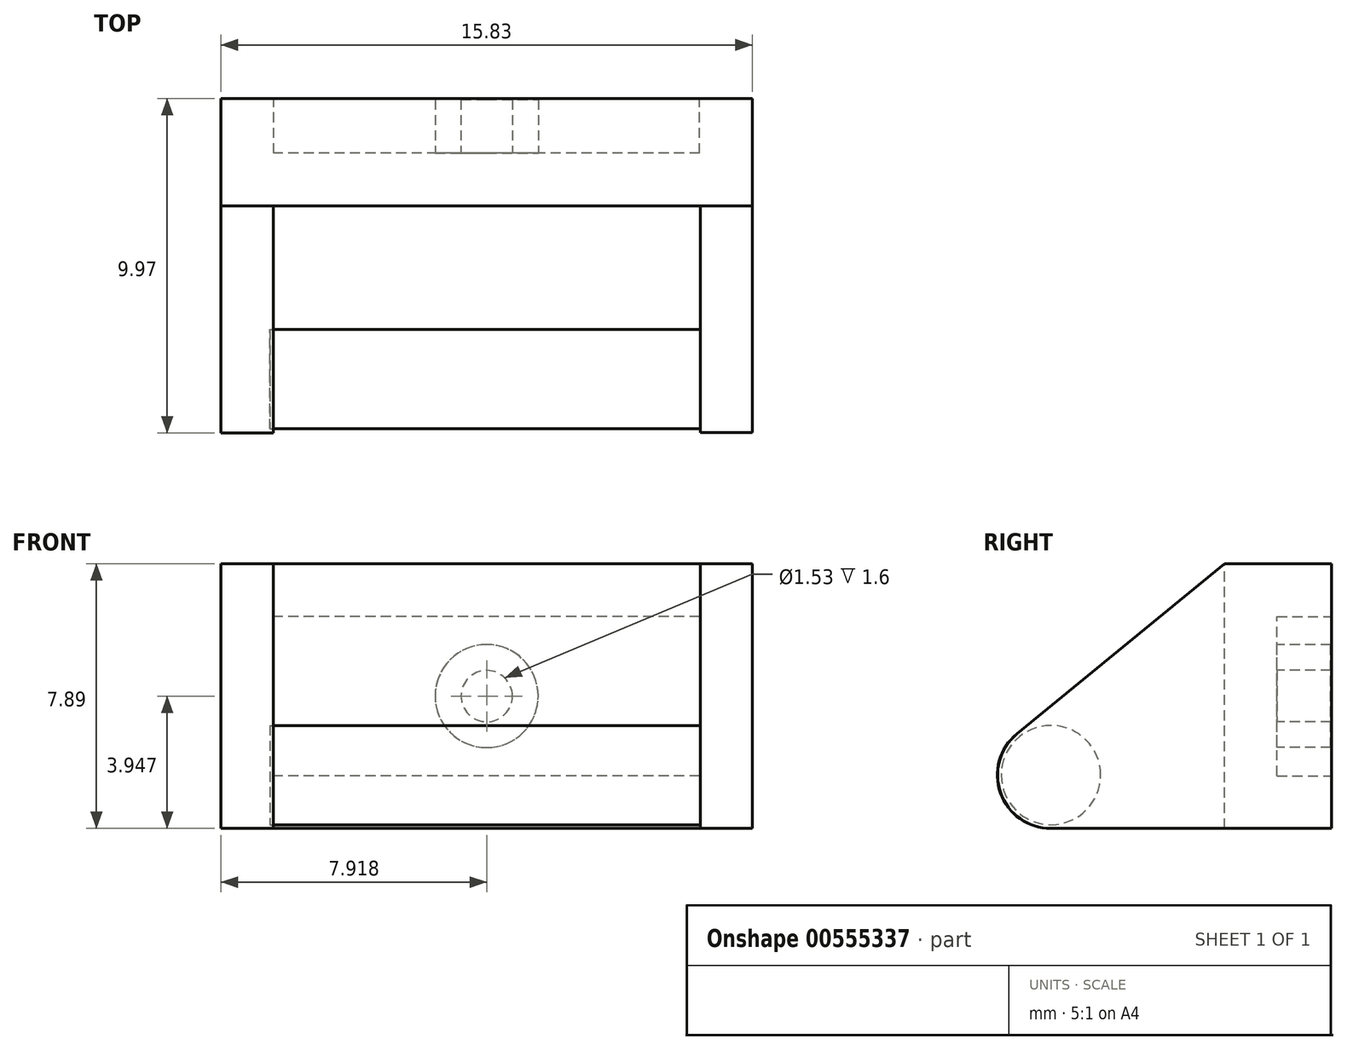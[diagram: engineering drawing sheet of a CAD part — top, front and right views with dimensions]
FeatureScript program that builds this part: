
annotation { "Feature Type Name" : "Feature", "Feature Type Description" : "" }
export const myFeature = defineFeature(function(context is Context, id is Id, definition is map)
    precondition{}
    {
        {
            var Q0;
            Q0=qCreatedBy(makeId("Front.planeOp"),FACE);
            var sketch = newSketch(context, id + "F0", { "sketchPlane" : qUnion([Q0])});
            skLineSegment(sketch, "E0.bottom", {"start": v(-20.1, 14.97) * mm, "end": v(-35.94, 14.97) * mm});
            skLineSegment(sketch, "E0.top", {"start": v(-20.1, 22.86) * mm, "end": v(-35.94, 22.86) * mm});
            skLineSegment(sketch, "E0.left", {"start": v(-20.1, 14.97) * mm, "end": v(-20.1, 22.86) * mm});
            skLineSegment(sketch, "E0.right", {"start": v(-35.94, 14.97) * mm, "end": v(-35.94, 22.86) * mm});
            skSolve(sketch);
        }
        {
            var Q0;
            Q0 = qSketchRegion(id + "F0", true);
            extrude(context, id + "F1", {"entities" : qUnion([Q0]), "depth" : 3.2 * mm, "offsetDistance" : 25 * mm});
        }
        {
            var Q0;
            Q0=makeQuery(id+"F1.opExtrude","SWEPT_FACE",FACE,{"disambiguationData":[OSD([sQuery(id+"F0.wireOp",EDGE,"E0.left")])]});
            var sketch = newSketch(context, id + "F2", { "sketchPlane" : qUnion([Q0])});
            skLineSegment(sketch, "E1", {"start": v(0, 14.97) * mm, "end": v(-12.8, 14.97) * mm});
            skLineSegment(sketch, "E2", {"start": v(-3.2, 22.86) * mm, "end": v(-12.81, 14.97) * mm});
            skSolve(sketch);
        }
        {
            var Q0;
            Q0 = qSketchRegion(id + "F2", true);
            var Q1;
            {var subQ2=sQuery(id+"F2.wireOp",EDGE,"E2");Q1=makeQuery(id+"F2.imprint","IMPRINT",FACE,{"disambiguationData":[TD([[makeQuery(id+"F2.imprint","IMPRINT",EDGE,{"derivedFrom":subQ2}),1.0]])]});}
            extrude(context, id + "F3", {"entities" : qUnion([Q0, Q1]), "operationType" : NewBodyOperationType.ADD, "oppositeDirection" : true, "depth" : 1.55 * mm, "offsetDistance" : 25 * mm});
        }
        {
            var Q0;
            Q0=makeQuery(id+"F3.opExtrude","SWEPT_EDGE",EDGE,{"disambiguationData":[OSD([sQuery(id+"F2.wireOp",EDGE,"E1"),sQuery(id+"F2.wireOp",EDGE,"E2")])]});
            fillet(context, id + "F4", {"entities" : qUnion([Q0]), "radius" : 1.59 * mm, "tangentPropagation" : true, "allowEdgeOverflow" : false});
        }
        {
            var Q0;
            Q0=makeQuery(id+"F1.opExtrude","SWEPT_FACE",FACE,{"disambiguationData":[OSD([sQuery(id+"F0.wireOp",EDGE,"E0.right")])]});
            var sketch = newSketch(context, id + "F5", { "sketchPlane" : qUnion([Q0])});
            skLineSegment(sketch, "E3", {"start": v(0, 14.97) * mm, "end": v(12.82, 14.97) * mm});
            skPoint(sketch, "E3.endSnap0", {"position": v(1.6, 14.97) * mm});
            skLineSegment(sketch, "E4", {"start": v(3.2, 22.86) * mm, "end": v(12.82, 14.97) * mm});
            skSolve(sketch);
        }
        {
            var Q0;
            Q0 = qSketchRegion(id + "F5", true);
            var Q1;
            {var subQ2=sQuery(id+"F5.wireOp",EDGE,"E4");Q1=makeQuery(id+"F5.imprint","IMPRINT",FACE,{"disambiguationData":[TD([[makeQuery(id+"F5.imprint","IMPRINT",EDGE,{"derivedFrom":subQ2}),-1.0]])]});}
            extrude(context, id + "F6", {"entities" : qUnion([Q0, Q1]), "oppositeDirection" : true, "depth" : 1.55 * mm, "offsetDistance" : 25 * mm});
        }
        {
            var Q0;
            Q0=makeQuery(id+"F6.opExtrude","SWEPT_EDGE",EDGE,{"disambiguationData":[OSD([sQuery(id+"F5.wireOp",EDGE,"E3"),sQuery(id+"F5.wireOp",EDGE,"E4")])]});
            fillet(context, id + "F7", {"entities" : qUnion([Q0]), "radius" : 1.59 * mm, "tangentPropagation" : true, "allowEdgeOverflow" : false});
        }
        {
            var Q0;
            Q0 = qSketchRegion(id + "F5", true);
            var Q1;
            Q1=makeQuery(id+"F6.opExtrude","CAP_FACE",FACE,{"disambiguationData":[OSD([sQuery(id+"F0.wireOp",EDGE,"E0.right"),sQuery(id+"F5.wireOp",EDGE,"E3"),sQuery(id+"F5.wireOp",EDGE,"E4")])],"isStart":true});
            extrude(context, id + "F8", {"entities" : qUnion([Q0, Q1]), "oppositeDirection" : true, "depth" : 1.55 * mm, "offsetDistance" : 25 * mm});
        }
        {
            var Q0;
            Q0=makeQuery(id+"F3.opExtrude","CAP_FACE",FACE,{"disambiguationData":[OSD([sQuery(id+"F0.wireOp",EDGE,"E0.left"),sQuery(id+"F2.wireOp",EDGE,"E1"),sQuery(id+"F2.wireOp",EDGE,"E2")])],"isStart":false});
            var sketch = newSketch(context, id + "F9", { "sketchPlane" : qUnion([Q0])});
            skCircle(sketch, "E5", {"center": v(8.37, 16.56) * mm, "radius": 1.48 * mm});
            skSolve(sketch);
        }
        {
            var Q0;
            Q0=makeQuery(id+"F9.imprint","IMPRINT",FACE,{"disambiguationData":[TD([[makeQuery(id+"F9.imprint","IMPRINT",EDGE,{"derivedFrom":sQuery(id+"F9.wireOp",EDGE,"E5")}),1.0]])]});
            extrude(context, id + "F10", {"entities" : qUnion([Q0]), "depth" : 12.83 * mm, "offsetDistance" : 25 * mm});
        }
        {
            var Q0;
            Q0=makeQuery(id+"F1.opExtrude","CAP_FACE",FACE,{"disambiguationData":[OSD([sQuery(id+"F0.wireOp",EDGE,"E0.bottom"),sQuery(id+"F0.wireOp",EDGE,"E0.top"),sQuery(id+"F0.wireOp",EDGE,"E0.left"),sQuery(id+"F0.wireOp",EDGE,"E0.right")])],"isStart":true});
            shell(context, id + "F11", {"entities" : qUnion([Q0]), "thickness" : 1.57 * mm});
        }
        {
            var Q0;
            Q0=makeQuery(id+"F11.opShell","OFFSET_FACE",FACE,{"disambiguationData":[OSD([sQuery(id+"F0.wireOp",EDGE,"E0.bottom"),sQuery(id+"F0.wireOp",EDGE,"E0.top"),sQuery(id+"F0.wireOp",EDGE,"E0.left"),sQuery(id+"F0.wireOp",EDGE,"E0.right")])]});
            var sketch = newSketch(context, id + "F12", { "sketchPlane" : qUnion([Q0])});
            skCircle(sketch, "E6", {"center": v(28.02, 18.92) * mm, "radius": 1.53 * mm});
            skPoint(sketch, "E6.centerSnap0", {"position": v(34.37, 18.92) * mm});
            skPoint(sketch, "E6.centerSnap1", {"position": v(28.02, 21.3) * mm});
            skCircle(sketch, "E7", {"center": v(28.02, 18.92) * mm, "radius": 0.77 * mm});
            skSolve(sketch);
        }
        {
            var Q0;
            Q0=makeQuery(id+"F12.imprint","IMPRINT",FACE,{"disambiguationData":[TD([[makeQuery(id+"F12.imprint","IMPRINT",EDGE,{"derivedFrom":sQuery(id+"F12.wireOp",EDGE,"E6")}),1.0]])]});
            extrude(context, id + "F13", {"entities" : qUnion([Q0]), "operationType" : NewBodyOperationType.ADD, "depth" : 1.6 * mm, "offsetDistance" : 25 * mm});
        }
    });
